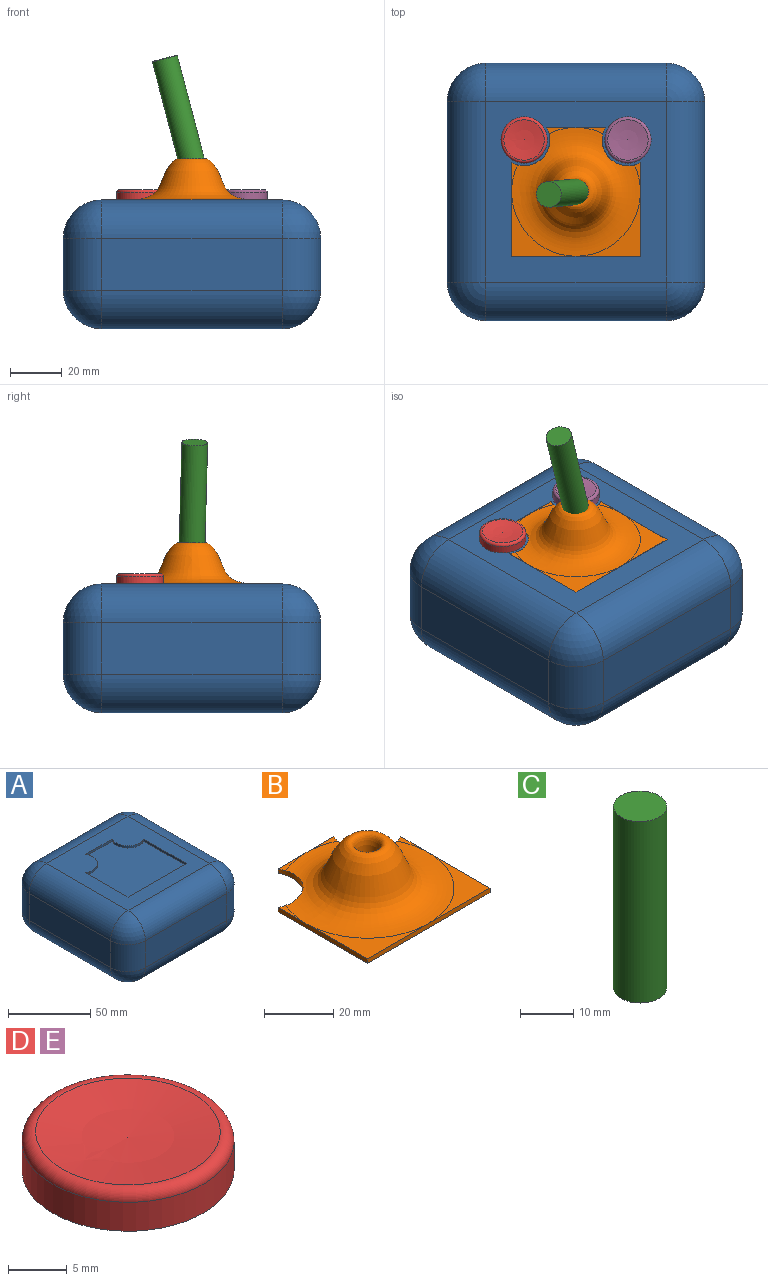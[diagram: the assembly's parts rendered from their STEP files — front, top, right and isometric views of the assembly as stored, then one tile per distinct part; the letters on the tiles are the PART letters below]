
ASSEMBLY  parts=5 mates=4
PART A: 37 faces, bbox 100x100x50 mm
  f0: plane 70x70mm, normal (0,0,1), area 2789.9mm2, adj f9,f10,f19,f20,f26,f27,f28,f29
  f1: plane 70x20mm, normal (0,1,0), area 1400mm2, adj f14,f19,f22,f25
  f2: plane 70x20mm, normal (-1,0,0), area 1400mm2, adj f11,f20,f21,f25
  f3: plane 70x20mm, normal (0,-1,0), area 1400mm2, adj f6,f10,f11,f12
  f4: plane 70x20mm, normal (1,0,0), area 1400mm2, adj f6,f9,f13,f14
  f5: plane 70x70mm, normal (0,0,-1), area 4900mm2, adj f12,f13,f21,f22
  f6: cylinder r=15mm len=20mm, axis (0,0,1), area 471.2mm2, adj f3,f4,f7,f8
  f7: sphere r=15mm, area 353.4mm2, adj f6,f9,f10
  f8: sphere r=15mm, area 353.4mm2, adj f6,f12,f13
  f9: cylinder r=15mm len=70mm, axis (0,-1,0), area 1649.3mm2, adj f0,f4,f7,f15
  f10: cylinder r=15mm len=70mm, axis (-1,0,0), area 1649.3mm2, adj f0,f3,f7,f16
  f11: cylinder r=15mm len=20mm, axis (0,0,-1), area 471.2mm2, adj f2,f3,f16,f17
  f12: cylinder r=15mm len=70mm, axis (1,0,0), area 1649.3mm2, adj f3,f5,f8,f17
  f13: cylinder r=15mm len=70mm, axis (0,1,0), area 1649.3mm2, adj f4,f5,f8,f18
  f14: cylinder r=15mm len=20mm, axis (0,0,-1), area 471.2mm2, adj f1,f4,f15,f18
  f15: sphere r=15mm, area 353.4mm2, adj f9,f14,f19
  f16: sphere r=15mm, area 353.4mm2, adj f10,f11,f20
  f17: sphere r=15mm, area 353.4mm2, adj f11,f12,f21
  f18: sphere r=15mm, area 353.4mm2, adj f13,f14,f22
  f19: cylinder r=15mm len=70mm, axis (1,0,0), area 1649.3mm2, adj f0,f1,f15,f23
  f20: cylinder r=15mm len=70mm, axis (0,1,0), area 1649.3mm2, adj f0,f2,f16,f23
  f21: cylinder r=15mm len=70mm, axis (0,-1,0), area 1649.3mm2, adj f2,f5,f17,f24
  f22: cylinder r=15mm len=70mm, axis (-1,0,0), area 1649.3mm2, adj f1,f5,f18,f24
  f23: sphere r=15mm, area 353.4mm2, adj f19,f20,f25
  f24: sphere r=15mm, area 353.4mm2, adj f21,f22,f25
  f25: cylinder r=15mm len=20mm, axis (0,0,1), area 471.2mm2, adj f1,f2,f23,f24
  f26: cylinder r=10mm len=12.54mm, axis (0,0,1), area 33.3mm2, adj f0,f27,f35,f36
  f27: cylinder r=10mm len=2.3mm, axis (0,0,1), area 4mm2, adj f0,f26,f28,f36
  f28: plane 22.82x1.6mm, normal (0,-1,0), area 36.5mm2, adj f0,f27,f29,f36
  f29: cylinder r=10mm len=2.3mm, axis (0,0,1), area 4mm2, adj f0,f28,f30,f36
  f30: cylinder r=10mm len=12.54mm, axis (0,0,1), area 33.3mm2, adj f0,f29,f31,f36
  f31: cylinder r=10mm len=2.3mm, axis (0,0,1), area 4mm2, adj f0,f30,f32,f36
  f32: plane 36.41x1.6mm, normal (1,0,0), area 58.3mm2, adj f0,f31,f33,f36
  f33: plane 50x1.6mm, normal (0,1,0), area 80mm2, adj f0,f32,f34,f36
  f34: plane 36.41x1.6mm, normal (-1,0,0), area 58.3mm2, adj f0,f33,f35,f36
  f35: cylinder r=10mm len=2.3mm, axis (0,0,1), area 4mm2, adj f0,f26,f34,f36
  f36: plane 50x50mm, normal (0,0,1), area 2110.1mm2, adj f26,f27,f28,f29,f30,f31,f32,f33
PART B: 15 faces, bbox 50x50x17.6 mm
  f0: plane 11.41x2.3mm, normal (0,0,1), area 8.8mm2, adj f9,f11,f14
  f1: plane 11.41x2.3mm, normal (0,0,1), area 8.8mm2, adj f9,f11,f13
  f2: plane 50x50mm, normal (0,0,-1), area 2110.1mm2, adj f6,f7,f8,f9,f13,f14
  f3: plane 11.41x2.3mm, normal (0,0,1), area 8.8mm2, adj f6,f11,f14
  f4: plane 11.41x2.3mm, normal (0,0,1), area 8.8mm2, adj f8,f11,f13
  f5: plane 25x25mm, normal (0,0,1), area 134.1mm2, adj f7,f8,f11
  f6: plane 36.41x1.6mm, normal (-1,0,0), area 58.3mm2, adj f2,f3,f7,f10,f14
  f7: plane 50x1.6mm, normal (0,-1,0), area 80mm2, adj f2,f5,f6,f8,f10
  f8: plane 36.41x1.6mm, normal (1,0,0), area 58.3mm2, adj f2,f4,f5,f7,f13
  f9: plane 22.82x1.6mm, normal (0,1,0), area 36.5mm2, adj f0,f1,f2,f13,f14
  f10: plane 25x25mm, normal (0,0,1), area 134.1mm2, adj f6,f7,f11
  f11: revolved ~50x50mm, area 2640.7mm2, adj f0,f1,f3,f4,f5,f10,f12,f13
  f12: plane 5.99x5.99mm, normal (0,0,1), area 28.2mm2, adj f11
  f13: cylinder r=10mm len=14.84mm, axis (0,0,1), area 48.1mm2, adj f1,f2,f4,f8,f9,f11
  f14: cylinder r=10mm len=14.84mm, axis (0,0,1), area 48.1mm2, adj f0,f2,f3,f6,f9,f11
PART C: 3 faces, bbox 10x10x41.7 mm
  f0: cylinder r=5mm len=41.7mm, axis (0,0,-1), area 1310mm2, adj f1,f2
  f1: plane 10x10mm, normal (0,0,1), area 78.5mm2, adj f0
  f2: plane 10x10mm, normal (0,0,-1), area 78.5mm2, adj f0
PART D: 4 faces, bbox 19.5x19.5x4 mm
  f0: cylinder r=9mm len=18mm, axis (0,0,-1), area 169.6mm2, adj f1,f3
  f1: torus R=8mm, axis (0,0,-1), area 93.4mm2, adj f0,f2
  f2: sphere r=50mm, area 194.3mm2, adj f1
  f3: plane 18x18mm, normal (0,0,-1), area 254.5mm2, adj f0
PART E: same geometry as D
PLACE A t=(91.2,-8.62,10.54)mm fixed
PLACE B t=(91.2,-8.62,58.94)mm
PLACE C rot(axis=(0.13,-0.95,-0.27),15.3deg) t=(91.2,-8.62,75.15)mm
PLACE D t=(71.04,11.54,60.54)mm
PLACE E t=(111.35,11.54,60.54)mm
MATE ball C.f0 <-> B.f11  axis (0.25,0.03,-0.97) through (91.2,-8.62,75.15)mm
MATE fastened A.f36 <-> B.f2  axis (0,0,-1) through (91.2,-8.62,58.94)mm
MATE fastened A.f29 <-> D.f0  axis (0,0,1) through (71.04,11.54,60.54)mm
MATE fastened A.f26 <-> E.f0  axis (0,0,1) through (111.35,11.54,60.54)mm
